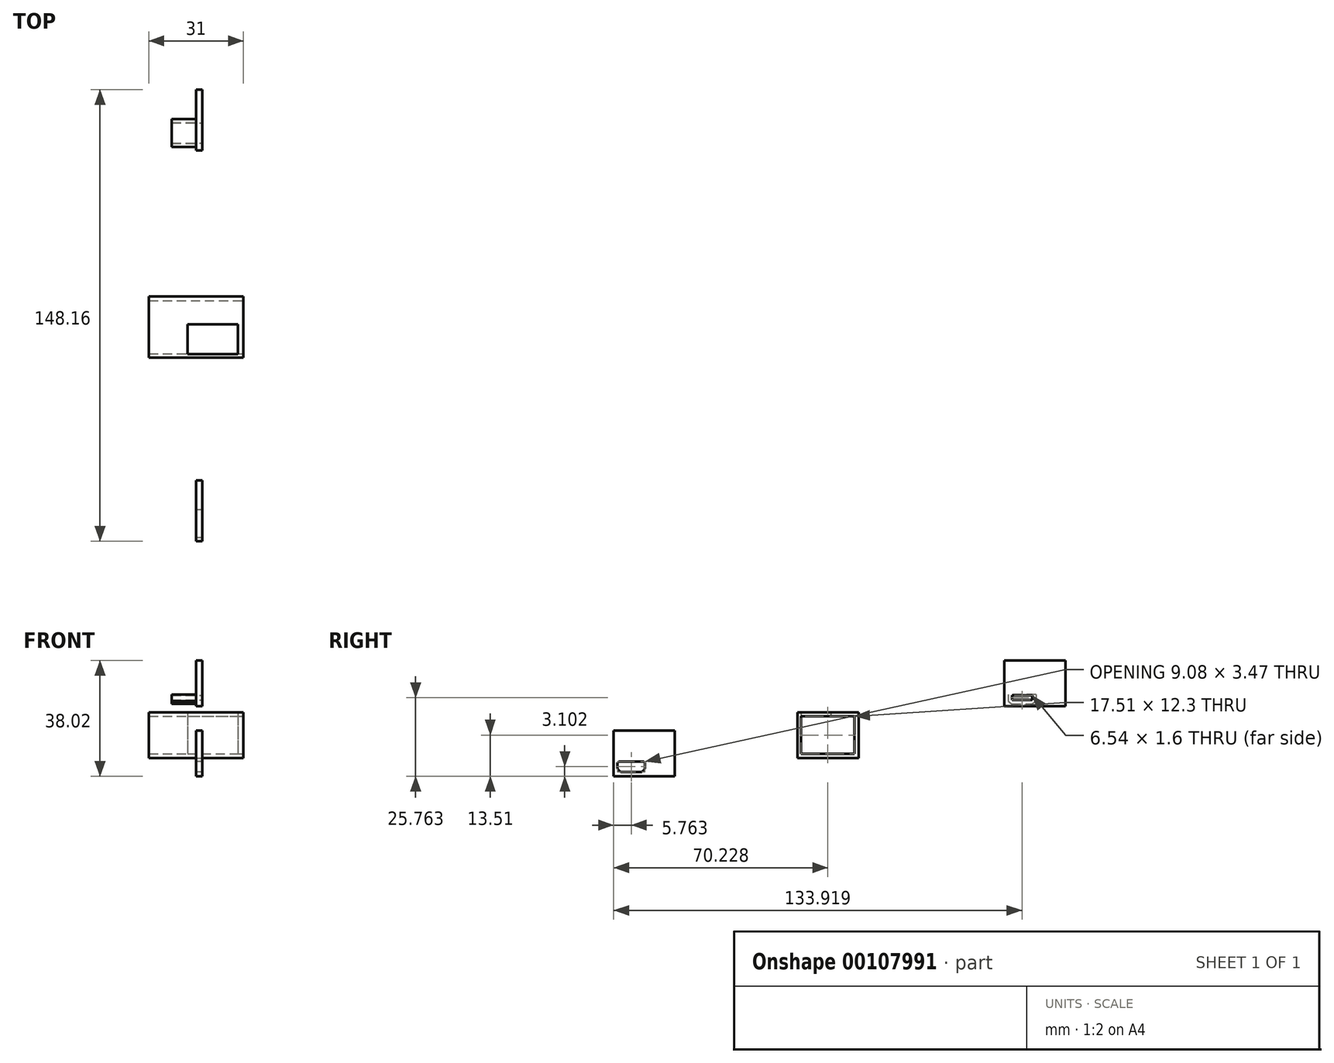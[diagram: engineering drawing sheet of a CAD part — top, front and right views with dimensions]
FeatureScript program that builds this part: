
annotation { "Feature Type Name" : "Feature", "Feature Type Description" : "" }
export const myFeature = defineFeature(function(context is Context, id is Id, definition is map)
    precondition{}
    {
        {
            var Q0;
            Q0=qCreatedBy(makeId("Top.planeOp"),FACE);
            var sketch = newSketch(context, id + "F0", { "sketchPlane" : qUnion([Q0])});
            skLineSegment(sketch, "E0.bottom", {"start": v(-15.5, -10) * mm, "end": v(15.5, -10) * mm});
            skLineSegment(sketch, "E0.top", {"start": v(-15.5, 10) * mm, "end": v(15.5, 10) * mm});
            skLineSegment(sketch, "E0.left", {"start": v(-15.5, -10) * mm, "end": v(-15.5, 10) * mm});
            skLineSegment(sketch, "E0.right", {"start": v(15.5, -10) * mm, "end": v(15.5, 10) * mm});
            skPoint(sketch, "E0.middle", {"position": v(0, 0) * mm});
            skPoint(sketch, "E1", {"position": v(5.5, -4) * mm});
            skLineSegment(sketch, "E2.bottom", {"start": v(-2.75, -8.85) * mm, "end": v(13.75, -8.85) * mm});
            skLineSegment(sketch, "E2.top", {"start": v(-2.75, 0.85) * mm, "end": v(13.75, 0.85) * mm});
            skLineSegment(sketch, "E2.left", {"start": v(-2.75, -8.85) * mm, "end": v(-2.75, 0.85) * mm});
            skLineSegment(sketch, "E2.right", {"start": v(13.75, -8.85) * mm, "end": v(13.75, 0.85) * mm});
            skSolve(sketch);
        }
        {
            var Q0;
            Q0=makeQuery(id+"F0.imprint","IMPRINT",FACE,{"disambiguationData":[TD([[makeQuery(id+"F0.imprint","IMPRINT",EDGE,{"derivedFrom":sQuery(id+"F0.wireOp",EDGE,"E0.bottom")}),1.0]])]});
            extrude(context, id + "F1", {"entities" : qUnion([Q0]), "depth" : 15 * mm});
        }
        {
            var Q0;
            Q0=makeQuery(id+"F1.opExtrude","SWEPT_FACE",FACE,{"disambiguationData":[OSD([sQuery(id+"F0.wireOp",EDGE,"E0.right")])]});
            var sketch = newSketch(context, id + "F2", { "sketchPlane" : qUnion([Q0])});
            skLineSegment(sketch, "E3.bottom", {"start": v(8.7, 1.38) * mm, "end": v(-8.82, 1.38) * mm});
            skLineSegment(sketch, "E3.top", {"start": v(8.7, 13.68) * mm, "end": v(-8.82, 13.68) * mm});
            skLineSegment(sketch, "E3.left", {"start": v(8.7, 1.38) * mm, "end": v(8.7, 13.68) * mm});
            skLineSegment(sketch, "E3.right", {"start": v(-8.82, 1.38) * mm, "end": v(-8.82, 13.68) * mm});
            skSolve(sketch);
        }
        {
            var Q0;
            Q0=makeQuery(id+"F2.imprint","IMPRINT",FACE,{"disambiguationData":[TD([[makeQuery(id+"F2.imprint","IMPRINT",EDGE,{"derivedFrom":sQuery(id+"F2.wireOp",EDGE,"E3.bottom")}),-1.0]])]});
            var Q1;
            Q1=makeQuery(id+"F1.opExtrude","SWEPT_FACE",FACE,{"disambiguationData":[OSD([sQuery(id+"F0.wireOp",EDGE,"E0.left")])]});
            extrude(context, id + "F3", {"entities" : qUnion([Q0]), "operationType" : NewBodyOperationType.REMOVE, "endBound" : BoundingType.UP_TO_SURFACE, "oppositeDirection" : true, "endBoundEntityFace" : qUnion([Q1]), "depth" : 25.4 * mm});
        }
        {
            var Q0;
            Q0=qCreatedBy(makeId("Right.planeOp"),FACE);
            var sketch = newSketch(context, id + "F4", { "sketchPlane" : qUnion([Q0])});
            skLineSegment(sketch, "E4.bottom", {"start": v(-70.29, -5.98) * mm, "end": v(-50.29, -5.98) * mm});
            skLineSegment(sketch, "E4.top", {"start": v(-70.29, 9.02) * mm, "end": v(-50.29, 9.02) * mm});
            skLineSegment(sketch, "E4.left", {"start": v(-70.29, -5.98) * mm, "end": v(-70.29, 9.02) * mm});
            skLineSegment(sketch, "E4.right", {"start": v(-50.29, -5.98) * mm, "end": v(-50.29, 9.02) * mm});
            skPoint(sketch, "E4.middle", {"position": v(-60.29, 1.52) * mm});
            skLineSegment(sketch, "E5.bottom", {"start": v(-59.99, -1.14) * mm, "end": v(-69.07, -1.14) * mm});
            skLineSegment(sketch, "E5.left", {"start": v(-59.99, -1.14) * mm, "end": v(-59.99, -3.64) * mm});
            skLineSegment(sketch, "E5.right", {"start": v(-69.07, -1.14) * mm, "end": v(-69.07, -3.64) * mm});
            skPoint(sketch, "E6", {"position": v(-67.92, -4.61) * mm});
            skPoint(sketch, "E7", {"position": v(-61.13, -4.61) * mm});
            skLineSegment(sketch, "E8", {"start": v(-69.07, -3.64) * mm, "end": v(-67.92, -4.61) * mm});
            skLineSegment(sketch, "E9", {"start": v(-59.99, -3.64) * mm, "end": v(-61.13, -4.61) * mm});
            skLineSegment(sketch, "E10", {"start": v(-67.92, -4.61) * mm, "end": v(-61.13, -4.61) * mm});
            skSolve(sketch);
        }
        {
            var Q0;
            Q0 = qSketchRegion(id + "F4", true);
            extrude(context, id + "F5", {"entities" : qUnion([Q0]), "depth" : 2 * mm});
        }
        {
            var Q0;
            Q0=makeQuery(id+"F4.imprint","IMPRINT",FACE,{"disambiguationData":[TD([[makeQuery(id+"F4.imprint","IMPRINT",EDGE,{"derivedFrom":sQuery(id+"F4.wireOp",EDGE,"E5.bottom")}),1.0]])]});
            extrude(context, id + "F6", {"entities" : qUnion([Q0]), "operationType" : NewBodyOperationType.REMOVE, "endBound" : BoundingType.THROUGH_ALL, "oppositeDirection" : true, "depth" : 25.4 * mm});
        }
        {
            var Q0;
            Q0=makeQuery(id+"F5.opExtrude","SWEPT_EDGE",EDGE,{"disambiguationData":[OSD([sQuery(id+"F4.wireOp",EDGE,"E5.left"),sQuery(id+"F4.wireOp",EDGE,"E9")])]});
            var Q1;
            Q1=makeQuery(id+"F5.opExtrude","SWEPT_EDGE",EDGE,{"disambiguationData":[OSD([sQuery(id+"F4.wireOp",EDGE,"E5.right"),sQuery(id+"F4.wireOp",EDGE,"E8")])]});
            fillet(context, id + "F7", {"entities" : qUnion([Q0, Q1]), "radius" : 1.52 * mm, "tangentPropagation" : true, "allowEdgeOverflow" : false});
        }
        {
            var Q0;
            Q0=makeQuery(id+"F5.opExtrude","SWEPT_EDGE",EDGE,{"disambiguationData":[OSD([sQuery(id+"F4.wireOp",EDGE,"E5.bottom"),sQuery(id+"F4.wireOp",EDGE,"E5.left")])]});
            var Q1;
            Q1=makeQuery(id+"F5.opExtrude","SWEPT_EDGE",EDGE,{"disambiguationData":[OSD([sQuery(id+"F4.wireOp",EDGE,"E5.bottom"),sQuery(id+"F4.wireOp",EDGE,"E5.right")])]});
            var Q2;
            Q2=makeQuery(id+"F5.opExtrude","SWEPT_EDGE",EDGE,{"disambiguationData":[OSD([sQuery(id+"F4.wireOp",EDGE,"E9"),sQuery(id+"F4.wireOp",EDGE,"E10")])]});
            var Q3;
            Q3=makeQuery(id+"F5.opExtrude","SWEPT_EDGE",EDGE,{"disambiguationData":[OSD([sQuery(id+"F4.wireOp",EDGE,"E8"),sQuery(id+"F4.wireOp",EDGE,"E10")])]});
            fillet(context, id + "F8", {"entities" : qUnion([Q0, Q1, Q2, Q3]), "radius" : 0.76 * mm, "tangentPropagation" : true, "allowEdgeOverflow" : false});
        }
        {
            var Q0;
            Q0=qCreatedBy(makeId("Right.planeOp"),FACE);
            var sketch = newSketch(context, id + "F9", { "sketchPlane" : qUnion([Q0])});
            skLineSegment(sketch, "E11.bottom", {"start": v(57.87, 17.04) * mm, "end": v(77.87, 17.04) * mm});
            skLineSegment(sketch, "E11.top", {"start": v(57.87, 32.04) * mm, "end": v(77.87, 32.04) * mm});
            skLineSegment(sketch, "E11.left", {"start": v(57.87, 17.04) * mm, "end": v(57.87, 32.04) * mm});
            skLineSegment(sketch, "E11.right", {"start": v(77.87, 17.04) * mm, "end": v(77.87, 32.04) * mm});
            skPoint(sketch, "E11.middle", {"position": v(67.87, 24.54) * mm});
            skLineSegment(sketch, "E12.bottom", {"start": v(68.17, 20.87) * mm, "end": v(59.09, 20.87) * mm});
            skLineSegment(sketch, "E12.left", {"start": v(68.17, 20.87) * mm, "end": v(68.17, 18.67) * mm});
            skLineSegment(sketch, "E12.right", {"start": v(59.09, 20.87) * mm, "end": v(59.09, 18.67) * mm});
            skPoint(sketch, "E13", {"position": v(60.23, 17.7) * mm});
            skPoint(sketch, "E14", {"position": v(67.03, 17.7) * mm});
            skLineSegment(sketch, "E15", {"start": v(59.09, 18.67) * mm, "end": v(60.23, 17.7) * mm});
            skLineSegment(sketch, "E16", {"start": v(68.17, 18.67) * mm, "end": v(67.03, 17.7) * mm});
            skLineSegment(sketch, "E17", {"start": v(60.23, 17.7) * mm, "end": v(67.03, 17.7) * mm});
            skLineSegment(sketch, "E18.bottom", {"start": v(66.9, 20.87) * mm, "end": v(60.36, 20.87) * mm});
            skLineSegment(sketch, "E19.bottom", {"start": v(60.36, 20.58) * mm, "end": v(66.9, 20.58) * mm});
            skLineSegment(sketch, "E19.top", {"start": v(60.36, 18.98) * mm, "end": v(66.9, 18.98) * mm});
            skLineSegment(sketch, "E19.left", {"start": v(60.36, 20.58) * mm, "end": v(60.36, 18.98) * mm});
            skLineSegment(sketch, "E19.right", {"start": v(66.9, 20.58) * mm, "end": v(66.9, 18.98) * mm});
            skSolve(sketch);
        }
        {
            var Q0;
            Q0 = qSketchRegion(id + "F9", true);
            extrude(context, id + "F10", {"entities" : qUnion([Q0]), "depth" : 2 * mm});
        }
        {
            var Q0;
            Q0=makeQuery(id+"F10.opExtrude","SWEPT_EDGE",EDGE,{"disambiguationData":[OSD([sQuery(id+"F9.wireOp",EDGE,"E12.left"),sQuery(id+"F9.wireOp",EDGE,"E16")])]});
            var Q1;
            Q1=makeQuery(id+"F10.opExtrude","SWEPT_EDGE",EDGE,{"disambiguationData":[OSD([sQuery(id+"F9.wireOp",EDGE,"E12.right"),sQuery(id+"F9.wireOp",EDGE,"E15")])]});
            fillet(context, id + "F11", {"entities" : qUnion([Q0, Q1]), "radius" : 1.52 * mm, "tangentPropagation" : true, "allowEdgeOverflow" : false});
        }
        {
            var Q0;
            Q0=makeQuery(id+"F10.opExtrude","SWEPT_EDGE",EDGE,{"disambiguationData":[OSD([sQuery(id+"F9.wireOp",EDGE,"E12.bottom"),sQuery(id+"F9.wireOp",EDGE,"E12.left")])]});
            var Q1;
            Q1=makeQuery(id+"F10.opExtrude","SWEPT_EDGE",EDGE,{"disambiguationData":[OSD([sQuery(id+"F9.wireOp",EDGE,"E12.bottom"),sQuery(id+"F9.wireOp",EDGE,"E12.right")])]});
            fillet(context, id + "F12", {"entities" : qUnion([Q0, Q1]), "radius" : 0.5 * mm, "tangentPropagation" : true, "allowEdgeOverflow" : false});
        }
        {
            var Q0;
            Q0=makeQuery(id+"F9.imprint","IMPRINT",FACE,{"disambiguationData":[TD([[makeQuery(id+"F9.imprint","IMPRINT",EDGE,{"derivedFrom":sQuery(id+"F9.wireOp",EDGE,"E12.bottom")}),1.0]])]});
            var Q1;
            Q1=makeQuery(id+"F10.opExtrude","CAP_FACE",FACE,{"disambiguationData":[OSD([sQuery(id+"F9.wireOp",EDGE,"E11.bottom"),sQuery(id+"F9.wireOp",EDGE,"E11.top"),sQuery(id+"F9.wireOp",EDGE,"E11.left"),sQuery(id+"F9.wireOp",EDGE,"E11.right"),sQuery(id+"F9.wireOp",EDGE,"E12.bottom"),sQuery(id+"F9.wireOp",EDGE,"E12.left"),sQuery(id+"F9.wireOp",EDGE,"E12.right"),sQuery(id+"F9.wireOp",EDGE,"E15"),sQuery(id+"F9.wireOp",EDGE,"E16"),sQuery(id+"F9.wireOp",EDGE,"E17")])],"isStart":false});
            var Q2;
            Q2=makeQuery(id+"F10.opExtrude","SWEPT_BODY",BODY,{"disambiguationData":[OSD([sQuery(id+"F9.wireOp",EDGE,"E11.bottom"),sQuery(id+"F9.wireOp",EDGE,"E11.top"),sQuery(id+"F9.wireOp",EDGE,"E11.left"),sQuery(id+"F9.wireOp",EDGE,"E11.right"),sQuery(id+"F9.wireOp",EDGE,"E12.bottom"),sQuery(id+"F9.wireOp",EDGE,"E12.left"),sQuery(id+"F9.wireOp",EDGE,"E12.right"),sQuery(id+"F9.wireOp",EDGE,"E15"),sQuery(id+"F9.wireOp",EDGE,"E16"),sQuery(id+"F9.wireOp",EDGE,"E17")])]});
            extrude(context, id + "F13", {"entities" : qUnion([Q0]), "operationType" : NewBodyOperationType.ADD, "oppositeDirection" : true, "depth" : 8 * mm, "hasSecondDirection" : true, "secondDirectionBound" : SecondDirectionBoundingType.UP_TO_SURFACE, "secondDirectionOppositeDirection" : false, "secondDirectionBoundEntityFace" : qUnion([Q1]), "secondDirectionBoundEntityBody" : qUnion([Q2]), "secondDirectionDepth" : 25.4 * mm});
        }
        {
            var Q0;
            Q0=makeQuery(id+"F0.imprint","IMPRINT",FACE,{"disambiguationData":[TD([[makeQuery(id+"F0.imprint","IMPRINT",EDGE,{"derivedFrom":sQuery(id+"F0.wireOp",EDGE,"E2.bottom")}),1.0]])]});
            var Q1;
            Q1=makeQuery(id+"F3.boolean.opBoolean","COPY",FACE,{"derivedFrom":makeQuery(id+"F3.opExtrude","SWEPT_FACE",FACE,{"disambiguationData":[OSD([sQuery(id+"F2.wireOp",EDGE,"E3.bottom")])]})});
            extrude(context, id + "F14", {"entities" : qUnion([Q0]), "operationType" : NewBodyOperationType.ADD, "endBound" : BoundingType.UP_TO_SURFACE, "endBoundEntityFace" : qUnion([Q1]), "depth" : 25.4 * mm});
        }
    });
